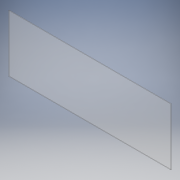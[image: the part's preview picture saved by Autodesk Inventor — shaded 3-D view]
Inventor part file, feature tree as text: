
AUTODESK INVENTOR PART (.ipt)
format: ipt  version: 2018 (Build 220112000, 112)  size: 93,696 bytes
history: native  units: in
note: dims shown in document units (in); Inventor stores cm internally (conversion verified against a paired STEP export)
features: extrude x1, sketch x1
ambient origin geometry x8: Origin, YZ Plane, XZ Plane, XY Plane, X Axis, Y Axis, Z Axis, Center Point
bodies: Solid1 (feature_tree)
feature tree (2):
  extrude  "Extrusion1"  Depth=14.9606in
  sketch  "Sketch1"  dims[d0=42.5197in d1=14.9606in d2=0.1575in d3=0.0in]
